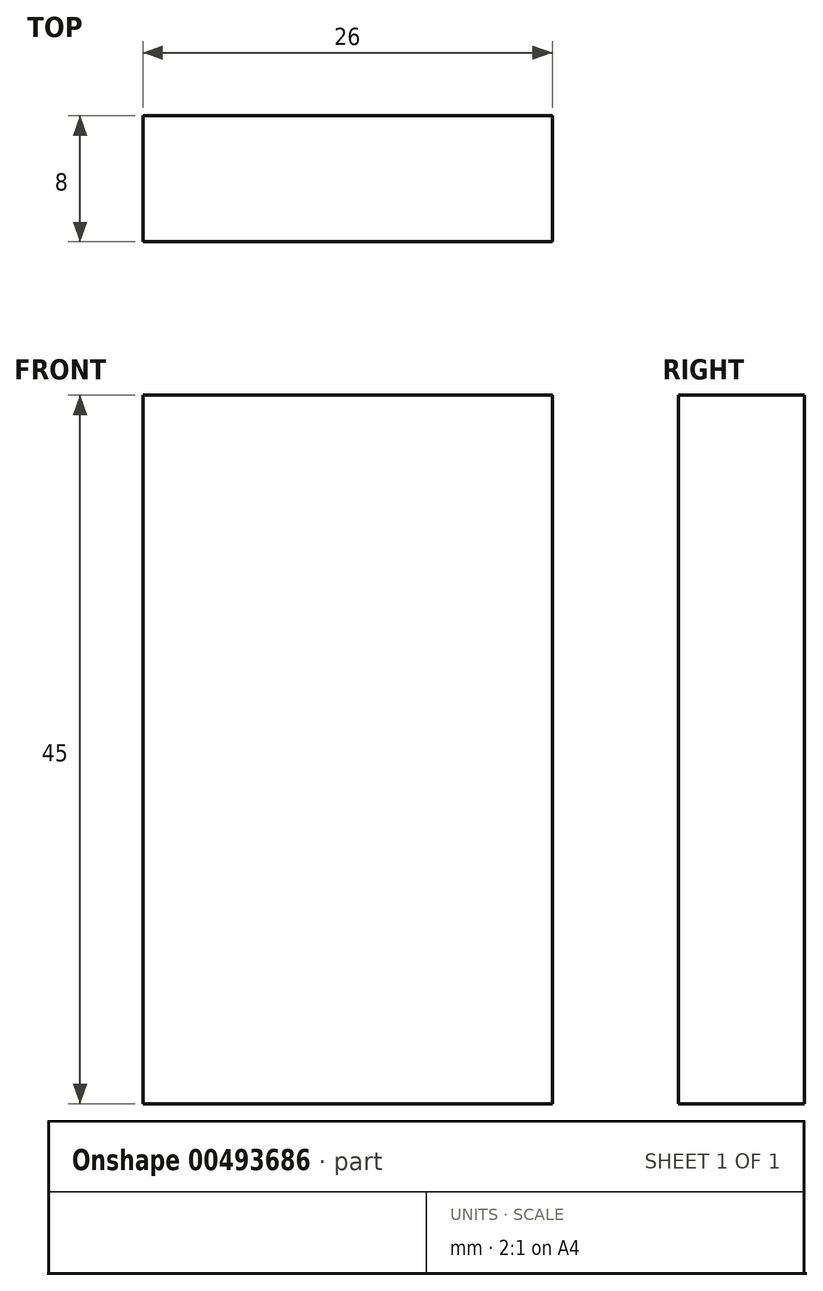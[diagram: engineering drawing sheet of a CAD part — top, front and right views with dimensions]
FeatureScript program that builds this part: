
annotation { "Feature Type Name" : "Feature", "Feature Type Description" : "" }
export const myFeature = defineFeature(function(context is Context, id is Id, definition is map)
    precondition{}
    {
        {
            var Q0;
            Q0=qCreatedBy(makeId("Front.planeOp"),FACE);
            var sketch = newSketch(context, id + "F0", { "sketchPlane" : qUnion([Q0])});
            skLineSegment(sketch, "E0.bottom", {"start": v(-13, 22.5) * mm, "end": v(13, 22.5) * mm});
            skLineSegment(sketch, "E0.top", {"start": v(-13, -22.5) * mm, "end": v(13, -22.5) * mm});
            skLineSegment(sketch, "E0.left", {"start": v(-13, 22.5) * mm, "end": v(-13, -22.5) * mm});
            skLineSegment(sketch, "E0.right", {"start": v(13, 22.5) * mm, "end": v(13, -22.5) * mm});
            skPoint(sketch, "E0.middle", {"position": v(0, 0) * mm});
            skSolve(sketch);
        }
        {
            var Q0;
            Q0=makeQuery(id+"F0.imprint","IMPRINT",FACE,{"disambiguationData":[TD([[makeQuery(id+"F0.imprint","IMPRINT",EDGE,{"derivedFrom":sQuery(id+"F0.wireOp",EDGE,"E0.bottom")}),-1.0]])]});
            extrude(context, id + "F1", {"entities" : qUnion([Q0]), "endBound" : BoundingType.SYMMETRIC, "depth" : 8 * mm});
        }
    });
